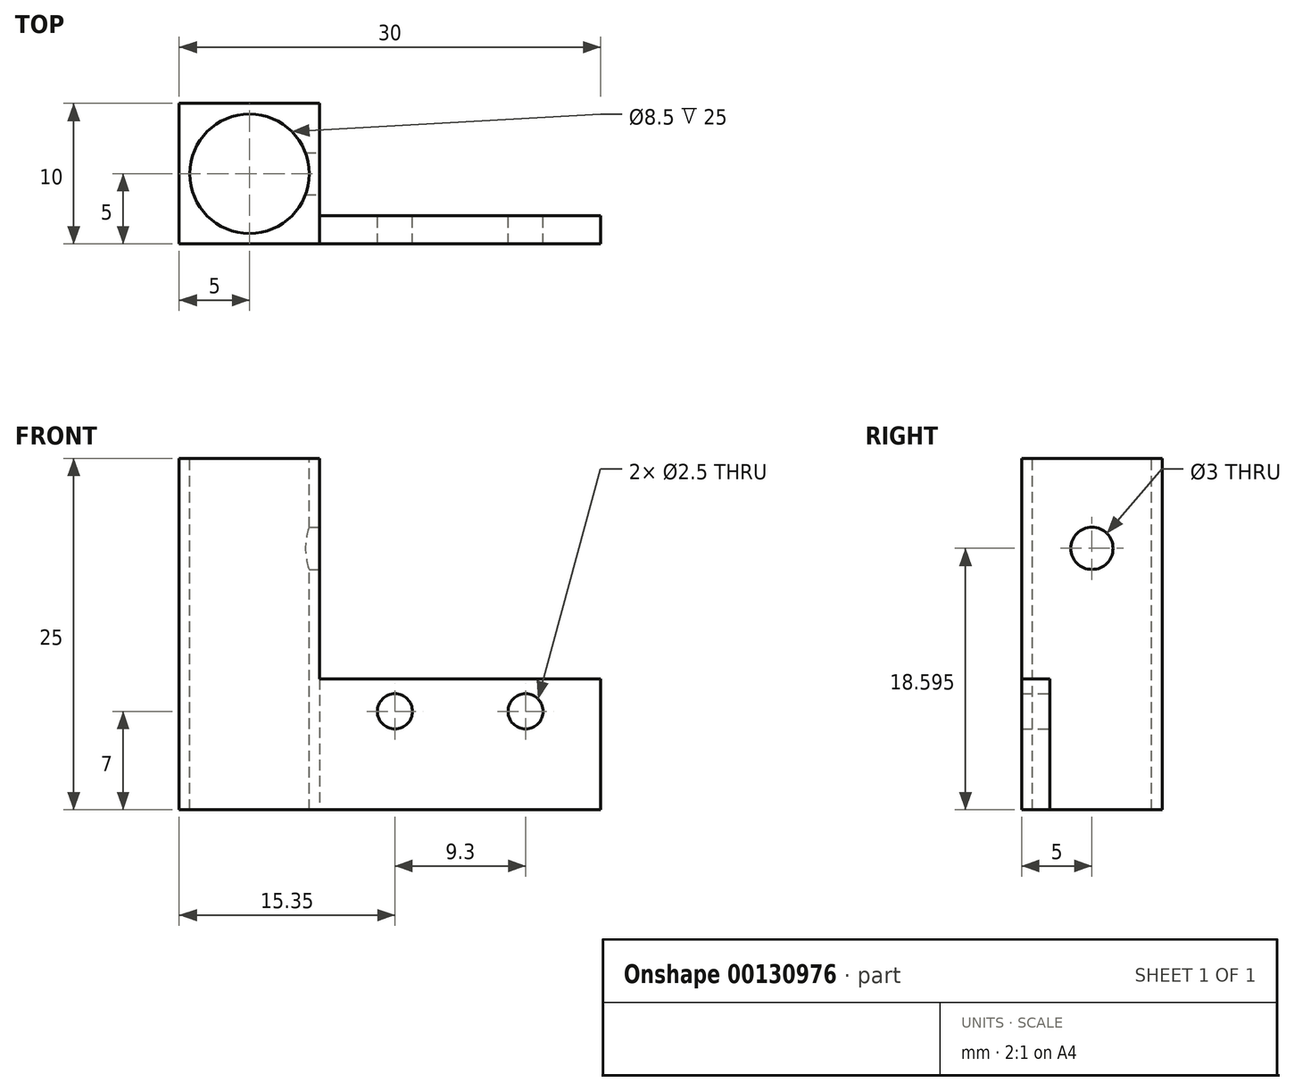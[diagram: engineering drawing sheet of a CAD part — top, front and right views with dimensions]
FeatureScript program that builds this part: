
annotation { "Feature Type Name" : "Feature", "Feature Type Description" : "" }
export const myFeature = defineFeature(function(context is Context, id is Id, definition is map)
    precondition{}
    {
        {
            var Q0;
            Q0=qCreatedBy(makeId("Top.planeOp"),FACE);
            var sketch = newSketch(context, id + "F0", { "sketchPlane" : qUnion([Q0])});
            skLineSegment(sketch, "E0.bottom", {"start": v(0, 0) * mm, "end": v(10, 0) * mm});
            skLineSegment(sketch, "E0.top", {"start": v(0, 10) * mm, "end": v(10, 10) * mm});
            skLineSegment(sketch, "E0.left", {"start": v(0, 0) * mm, "end": v(0, 10) * mm});
            skLineSegment(sketch, "E0.right", {"start": v(10, 0) * mm, "end": v(10, 10) * mm});
            skSolve(sketch);
        }
        {
            var Q0;
            Q0 = qSketchRegion(id + "F0", true);
            extrude(context, id + "F1", {"entities" : qUnion([Q0]), "depth" : 25 * mm});
        }
        {
            var Q0;
            Q0=makeQuery(id+"F1.opExtrude","CAP_FACE",FACE,{"disambiguationData":[OSD([sQuery(id+"F0.wireOp",EDGE,"E0.bottom"),sQuery(id+"F0.wireOp",EDGE,"E0.top"),sQuery(id+"F0.wireOp",EDGE,"E0.left"),sQuery(id+"F0.wireOp",EDGE,"E0.right")])],"isStart":false});
            var sketch = newSketch(context, id + "F2", { "sketchPlane" : qUnion([Q0])});
            skLineSegment(sketch, "E1", {"start": v(5, 10) * mm, "end": v(5, 0) * mm});
            skLineSegment(sketch, "E2", {"start": v(10, 5) * mm, "end": v(0, 5) * mm});
            skCircle(sketch, "E3", {"center": v(5, 5) * mm, "radius": 4.25 * mm});
            skSolve(sketch);
        }
        {
            var Q0;
            Q0 = qSketchRegion(id + "F2", true);
            var Q1;
            Q1=sQuery(id+"F2.wireOp",EDGE,"E3");
            extrude(context, id + "F3", {"entities" : qUnion([Q0]), "operationType" : NewBodyOperationType.REMOVE, "surfaceEntities" : qUnion([Q1]), "endBound" : BoundingType.THROUGH_ALL, "oppositeDirection" : true, "depth" : 25 * mm});
        }
        {
            var Q0;
            Q0=makeQuery(id+"F1.opExtrude","SWEPT_FACE",FACE,{"disambiguationData":[OSD([sQuery(id+"F0.wireOp",EDGE,"E0.right")])]});
            var sketch = newSketch(context, id + "F4", { "sketchPlane" : qUnion([Q0])});
            skLineSegment(sketch, "E4.bottom", {"start": v(0, 9.3) * mm, "end": v(2, 9.3) * mm});
            skLineSegment(sketch, "E4.top", {"start": v(0, 0) * mm, "end": v(2, 0) * mm});
            skLineSegment(sketch, "E4.left", {"start": v(0, 9.3) * mm, "end": v(0, 0) * mm});
            skLineSegment(sketch, "E4.right", {"start": v(2, 9.3) * mm, "end": v(2, 0) * mm});
            skSolve(sketch);
        }
        {
            var Q0;
            Q0 = qSketchRegion(id + "F4", true);
            extrude(context, id + "F5", {"entities" : qUnion([Q0]), "operationType" : NewBodyOperationType.ADD, "depth" : 20 * mm});
        }
        {
            var Q0;
            Q0=makeQuery(id+"F5.opExtrude","SWEPT_FACE",FACE,{"disambiguationData":[OSD([sQuery(id+"F4.wireOp",EDGE,"E4.right")])]});
            var sketch = newSketch(context, id + "F6", { "sketchPlane" : qUnion([Q0])});
            skLineSegment(sketch, "E5", {"start": v(-10, 7) * mm, "end": v(-30, 7) * mm});
            skLineSegment(sketch, "E6", {"start": v(-20, 9.3) * mm, "end": v(-20, 0) * mm});
            skPoint(sketch, "E7", {"position": v(-15.35, 7) * mm});
            skPoint(sketch, "E8", {"position": v(-24.65, 7) * mm});
            skSolve(sketch);
        }
        {
            var Q0;
            Q0=sQuery(id+"F6.wireOp",VERTEX,"E7");
            var Q1;
            Q1=sQuery(id+"F6.wireOp",VERTEX,"E8");
            var Q2;
            Q2=makeQuery(id+"F1.opExtrude","SWEPT_BODY",BODY,{"disambiguationData":[OSD([sQuery(id+"F0.wireOp",EDGE,"E0.bottom"),sQuery(id+"F0.wireOp",EDGE,"E0.top"),sQuery(id+"F0.wireOp",EDGE,"E0.left"),sQuery(id+"F0.wireOp",EDGE,"E0.right")])]});
            hole(context, id + "F7", {"style" : HoleStyle.SIMPLE, "endStyle" : HoleEndStyle.THROUGH, "holeDiameter" : 2.5 * mm, "locations" : qUnion([Q0, Q1]), "scope" : qUnion([Q2]), "isTappedThrough" : true});
        }
        {
            var Q0;
            Q0=makeQuery(id+"F1.opExtrude","SWEPT_FACE",FACE,{"disambiguationData":[OSD([sQuery(id+"F0.wireOp",EDGE,"E0.right")])]});
            var sketch = newSketch(context, id + "F8", { "sketchPlane" : qUnion([Q0])});
            skLineSegment(sketch, "E9", {"start": v(5, 25) * mm, "end": v(5, 0) * mm});
            skPoint(sketch, "E10", {"position": v(5, 18.6) * mm});
            skSolve(sketch);
        }
        {
            var Q0;
            Q0=sQuery(id+"F8.wireOp",VERTEX,"E10");
            var Q1;
            Q1=makeQuery(id+"F1.opExtrude","SWEPT_BODY",BODY,{"disambiguationData":[OSD([sQuery(id+"F0.wireOp",EDGE,"E0.bottom"),sQuery(id+"F0.wireOp",EDGE,"E0.top"),sQuery(id+"F0.wireOp",EDGE,"E0.left"),sQuery(id+"F0.wireOp",EDGE,"E0.right")])]});
            hole(context, id + "F9", {"style" : HoleStyle.SIMPLE, "endStyle" : HoleEndStyle.BLIND, "holeDiameter" : 3 * mm, "holeDepth" : 5 * mm, "locations" : qUnion([Q0]), "scope" : qUnion([Q1])});
        }
    });
